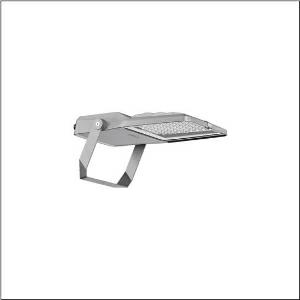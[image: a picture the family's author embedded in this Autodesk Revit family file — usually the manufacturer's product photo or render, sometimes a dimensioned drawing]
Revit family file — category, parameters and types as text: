
# Revit family: floodlight_fl_21_iq_mini___pl61_5xa7772d2c1a_0e67
name_source: partatom
category: Lighting Fixtures
units: mm (PartAtom-declared; Revit-internal decimal feet)

## family parameters
Cut with Voids When Loaded = No
Host = Face
Light Source = No
Part Type = Normal
Room Calculation Point = No
Round Connector Dimension = Use Diameter
Shared = No

## types (1)
- --- (1 x LED, 17500 lm, 143 W, 3000K)
    Apparent Load = 143 VA
    CIE Flux Codes = 33 65 98 100 100
    Color Rendering = 70
    Color Temperature = 3000K
    Default Elevation = 1800 mm
    Description = Floodlight FL 21 iQ mini, floodlight, primary light control with lens, of PMMA, primary optical cover: protective disc, of toughened safety glass, transparent, light distribution: PL61, light emission: direct distribution, installation type: surface-mounted, LED, High Power LED, rated luminous flux: 17.500lm, luminous efficacy: 122lm/W, light colour: 730, colour temperature: 3000K, control gear: iQ Street-Remote/DALI, control: Street-Remote, Auto-Match, Temp-Guard, Night-Set, Smart-Wire, Desk-Remote (wireless, voltage-free reading and setting of iQ features in the workshop via application-optimized NFC function/RFID function), optimised constant luminous flux control (CLO 2.0), with terminal, 6-pole, mains connection: 220..240V, AC, 50/60Hz, start of lifetime: 143W, end of service life: 152W, reduction: 61W, luminaire housing, of diecast aluminium, powder-coated, Siteco® metallic grey (DB 702S), corrosivity category C5 mid according to DIN EN ISO 12944, suitable for swimming pools, chlorine-resistant, sealing non-destructively replaceable, mounting bracket, of steel, galvanised, powder-coated, Siteco® metallic grey (DB 702S), protection rating (complete): IP66, insulation class (complete): insulation class II (safety insulation), certification: CE, ENEC, VDE, protection symbol: D, impact resistance: IK08, permissible operating ambient temperature: -40..+40°C, permissible operating ambient temperature for outdoor applications: -40..+50°C, standard: DIN EN 12944, LABS conformity tested according to VDMA 24364:2018-05, packaging unit: 1 piece

Light Distribution: PL61
    Height = 70 mm
    Lamp = 1 x LED
    Lamp Light Flux = 17500 lm
    Lamp Power = 143 W
    Lamp count = 1
    Length = 485 mm
    Luminous efficacy = 122 lm/W
    Manufacturer = Siteco
    ModVariant = No
    Model = 5XA7772D2C1A
    Number of Poles = 1
    OnlyDefault = Yes
    Power Factor = 1
    Product Name = Floodlight FL 21 iQ mini | PL61
    Product group = floodlight | pylon annexe
    ProductGroupID = 6200
    Protection Class = Protection class II
    Protection Degree = IP 66
    RLX_Detail_Level = 1
    RLX_Emergency_Light_Flux = 0 lm
    RLX_Emergency_Type = 0
    RLX_Emergency_Type_DB = No
    RlxData = <blob elided: 96609 chars, md5=2837c58d>
    Socket = socket
    Standby Power = 0 W
    System Light Flux = 17500 lm
    System Power = 143 W
    Type Comments = factory setting: luminous flux: 100 % | dim-lin: 254 | 730 mA
    Type Image = l_1006845.jpg
    URL = http://relux.com
    VarID = @adj_172528
    Voltage = 0 V
    Weight = 0.00 kg
    Width = 337 mm

## geometry (parser evidence)
native form markers: Blend x4, Sweep x14
no freeform markers — native parametric forms only
